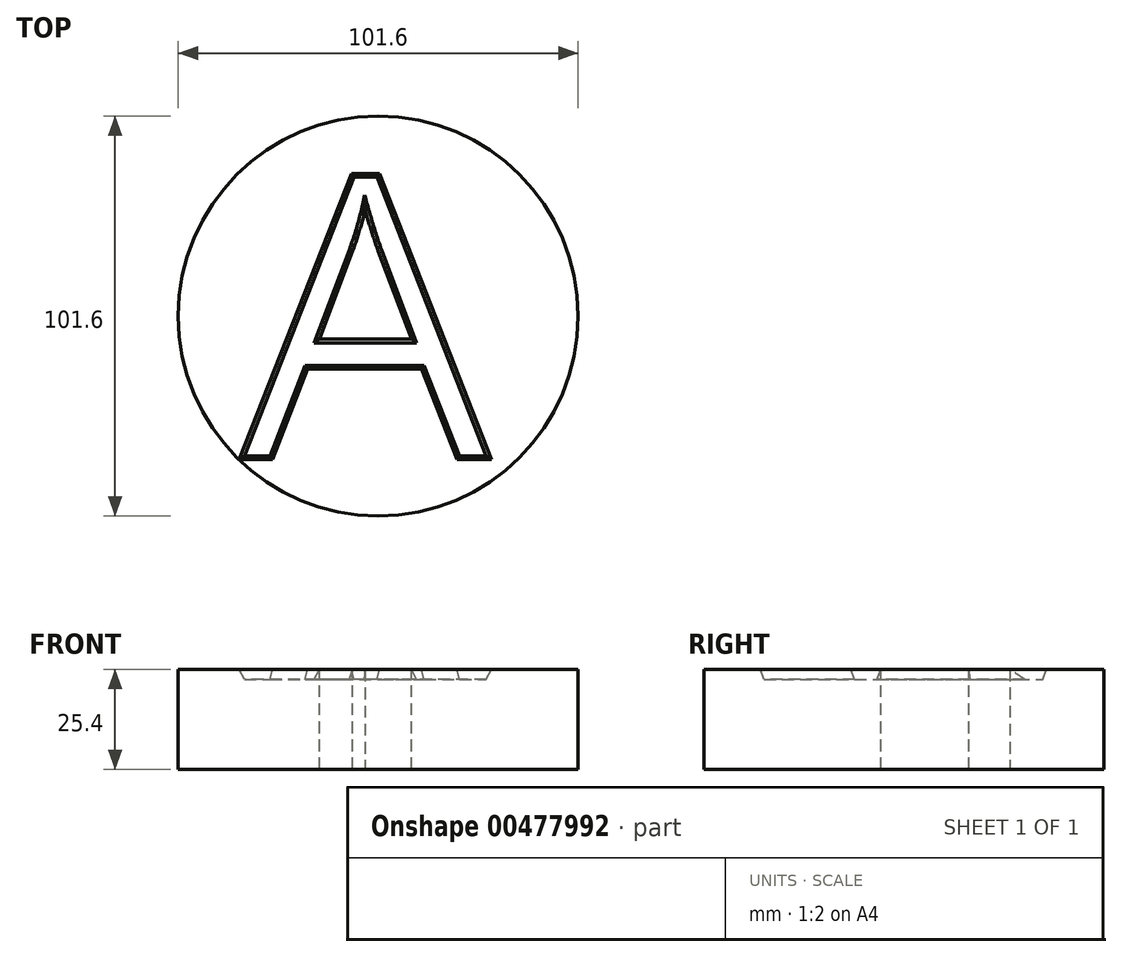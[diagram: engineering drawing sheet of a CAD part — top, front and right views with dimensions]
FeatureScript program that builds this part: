
annotation { "Feature Type Name" : "Feature", "Feature Type Description" : "" }
export const myFeature = defineFeature(function(context is Context, id is Id, definition is map)
    precondition{}
    {
        {
            var Q0;
            Q0=qCreatedBy(makeId("Top.planeOp"),FACE);
            var sketch = newSketch(context, id + "F0", { "sketchPlane" : qUnion([Q0])});
            skCircle(sketch, "E0", {"center": v(0, 0) * mm, "radius": 50.8 * mm});
            skSolve(sketch);
        }
        {
            var Q0;
            Q0=makeQuery(id+"F0.imprint","IMPRINT",FACE,{"disambiguationData":[TD([[makeQuery(id+"F0.imprint","IMPRINT",EDGE,{"derivedFrom":sQuery(id+"F0.wireOp",EDGE,"E0")}),1.0]])]});
            extrude(context, id + "F1", {"entities" : qUnion([Q0]), "depth" : 25.4 * mm});
        }
        {
            var Q0;
            Q0=makeQuery(id+"F1.opExtrude","CAP_FACE",FACE,{"disambiguationData":[OSD([sQuery(id+"F0.wireOp",EDGE,"E0")])],"isStart":false});
            var sketch = newSketch(context, id + "F2", { "sketchPlane" : qUnion([Q0])});
            skText(sketch, "E1", { "text": "A\n", "fontName": "OpenSans-Regular.ttf"});
            const initialGuessF2  = {"E1": [-0.03535, -0.03648, 1, 0, 0.07297]};
            skSetInitialGuess(sketch, initialGuessF2);
            skSolve(sketch);
        }
        {
            var Q0;
            Q0 = qSketchRegion(id + "F2", true);
            extrude(context, id + "F3", {"entities" : qUnion([Q0]), "operationType" : NewBodyOperationType.REMOVE, "oppositeDirection" : true, "depth" : 2.54 * mm, "hasDraft" : true, "draftAngle" : 20 * degree, "draftPullDirection" : true});
        }
        {
            var Q0;
            Q0=makeQuery(id+"F3.boolean.opBoolean","SPLIT",FACE,{"disambiguationData":[TD([makeQuery(id+"F3.opExtrude","SWEPT_FACE",FACE,{"disambiguationData":[OSD([sQuery(id+"F2.wireOp",EDGE,"E1.sketch_text.stroke-8")])]})])],"derivedFrom":makeQuery(id+"F1.opExtrude","CAP_FACE",FACE,{"disambiguationData":[OSD([sQuery(id+"F0.wireOp",EDGE,"E0")])],"isStart":false})});
            extrude(context, id + "F4", {"entities" : qUnion([Q0]), "operationType" : NewBodyOperationType.REMOVE, "oppositeDirection" : true, "depth" : 25.4 * mm});
        }
    });
